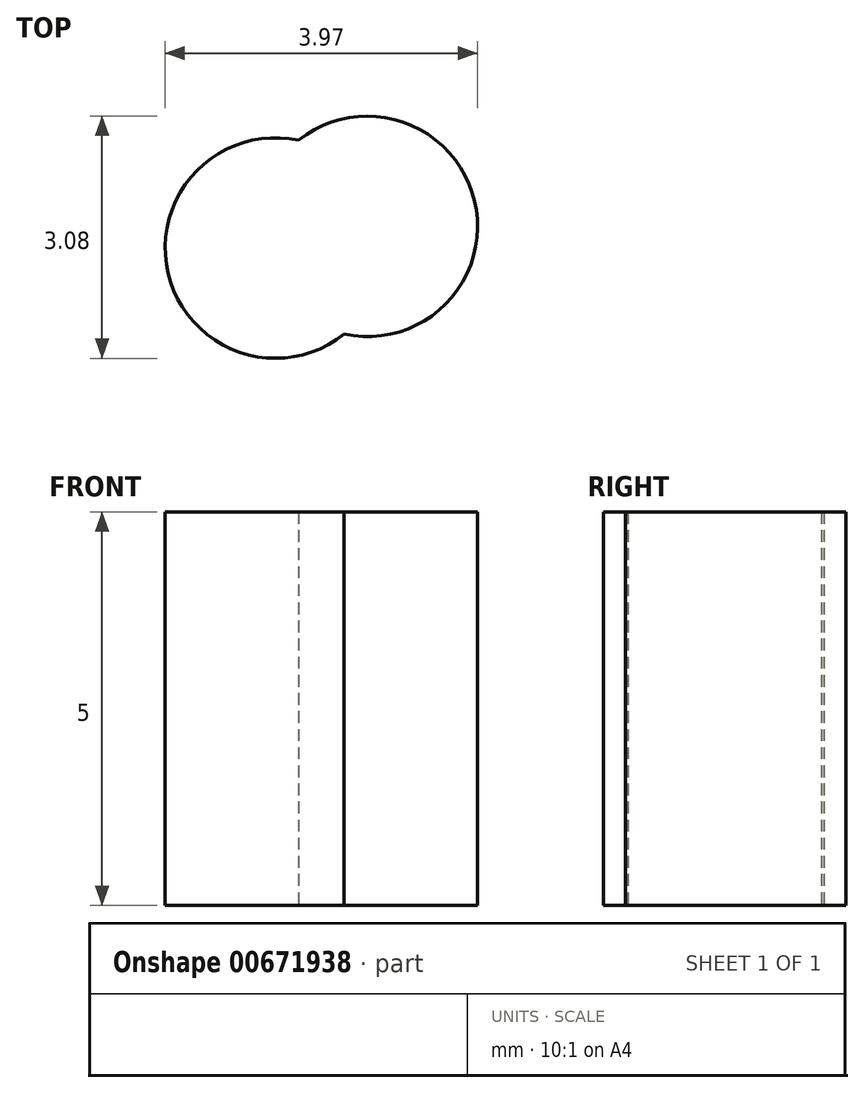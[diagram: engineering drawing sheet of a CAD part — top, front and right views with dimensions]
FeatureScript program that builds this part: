
annotation { "Feature Type Name" : "Feature", "Feature Type Description" : "" }
export const myFeature = defineFeature(function(context is Context, id is Id, definition is map)
    precondition{}
    {
        {
            var Q0;
            Q0=qCreatedBy(makeId("Top.planeOp"),FACE);
            var sketch = newSketch(context, id + "F0", { "sketchPlane" : qUnion([Q0])});
            skCircle(sketch, "E0", {"center": v(0.55, 0.13) * mm, "radius": 1.4 * mm});
            skCircle(sketch, "E1", {"center": v(-0.62, -0.15) * mm, "radius": 1.4 * mm});
            skSolve(sketch);
        }
        {
            var Q0;
            {var subQ0=sQuery(id+"F0.wireOp",EDGE,"E1");var subQ1=sQuery(id+"F0.wireOp",EDGE,"E0");var subQ2=makeQuery(id+"F0.imprint","INTERSECT",VERTEX,{"disambiguationData":[OD(0.0)],"derivedFrom":[subQ1,subQ0]});Q0=makeQuery(id+"F0.imprint","IMPRINT",FACE,{"disambiguationData":[TD([[makeQuery(id+"F0.imprint","IMPRINT",EDGE,{"disambiguationData":[TD([[subQ2,1.0]])],"derivedFrom":subQ1}),-1.0]])]});}
            var Q1;
            {var subQ0=sQuery(id+"F0.wireOp",EDGE,"E1");var subQ1=sQuery(id+"F0.wireOp",EDGE,"E0");var subQ2=makeQuery(id+"F0.imprint","INTERSECT",VERTEX,{"disambiguationData":[OD(0.0)],"derivedFrom":[subQ1,subQ0]});Q1=makeQuery(id+"F0.imprint","IMPRINT",FACE,{"disambiguationData":[TD([[makeQuery(id+"F0.imprint","IMPRINT",EDGE,{"disambiguationData":[TD([[subQ2,-1.0]])],"derivedFrom":subQ1}),1.0]])]});}
            var Q2;
            {var subQ0=sQuery(id+"F0.wireOp",EDGE,"E1");var subQ1=sQuery(id+"F0.wireOp",EDGE,"E0");var subQ2=makeQuery(id+"F0.imprint","INTERSECT",VERTEX,{"disambiguationData":[OD(0.0)],"derivedFrom":[subQ1,subQ0]});Q2=makeQuery(id+"F0.imprint","IMPRINT",FACE,{"disambiguationData":[TD([[makeQuery(id+"F0.imprint","IMPRINT",EDGE,{"disambiguationData":[TD([[subQ2,1.0]])],"derivedFrom":subQ1}),1.0]])]});}
            extrude(context, id + "F1", {"entities" : qUnion([Q0, Q1, Q2]), "depth" : 5 * mm, "offsetDistance" : 25 * mm});
        }
    });
